# Revit family: Electronics_Masking-Loudspeakers_Biamp_Cambridge_Window-Door-Wall-Masker_DS2500__
name_source: partatom
category: Communication Devices
units: mm (PartAtom-declared; Revit-internal decimal feet)

## family parameters
Cut with Voids When Loaded = No
Host = Face
Maintain Annotation Orientation = No
OmniClass Number = 23.85.10.11.11
OmniClass Title = Sound and Signal Devices
Part Type = Normal
Room Calculation Point = No
Round Connector Dimension = Use Diameter
Shared = No

## types (2) — shared parameters
Default Elevation = 48 "
Depth = 5 "
Description = Dynasound® DS2500 Window, Door, Wall Masker for SCIF / Secure Room
Driver = Non-conventional security type
Height = 1.34 "
Manufacturer = Biamp
Model = DS2500
Product Documentation Link = https://downloads.biamp.com
Product Page URL = https://www.biamp.com
Product data url = https://www.bimobject.com
Transformer = Primary 70.7v, Secondary 8 Ohms, Switch Positions: 1/8,1/4, 1/2,1,2,4 watts
URL = https://www.biamp.com
Weight = 2.00 lbf
Width = 5 "

## per-type parameters (varying)
| type | Housing Material |
| DS2500 Black | Biamp - Plastic - Black |
| DS2500 Beige | Biamp - Plastic - Beige |

## geometry (parser evidence)
native form markers: Sweep x3
no freeform markers — native parametric forms only
